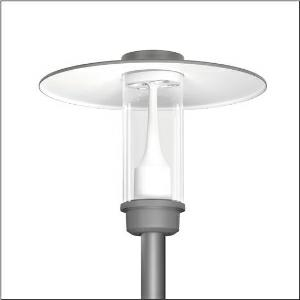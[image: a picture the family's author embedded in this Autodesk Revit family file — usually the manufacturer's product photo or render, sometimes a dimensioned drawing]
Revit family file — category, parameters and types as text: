
# Revit family: litepole_2_iq___st1_2a_5xa5425af14h_a18f
name_source: partatom
category: Lighting Fixtures
units: mm (PartAtom-declared; Revit-internal decimal feet)

## family parameters
Cut with Voids When Loaded = No
Host = Face
Light Source = No
Part Type = Normal
Room Calculation Point = No
Round Connector Dimension = Use Diameter
Shared = No

## types (1)
- --- (1 x LED, 1550 lm, 12.9 W, 2200K)
    Apparent Load = 13 VA
    CIE Flux Codes = 22 60 92 98 100
    Color Rendering = 70
    Color Temperature = 2200K
    Default Elevation = 1800 mm
    Description = Litepole 2 iQ, mast luminaire, Module 540 iQ-SR, primary light control with 3 zone facetted reflector, of plastic, silver coated, highly specular, structured, primary optical cover: cover, of PMMA, transparent, light distribution: ST1.2a, light emission: direct distribution, primary light characteristic: asymmetric, installation type: post-top, LED, High Power LED, rated luminous flux: 1.550lm, luminous efficacy: 120lm/W, light colour: 722, colour temperature: 2200K, control gear: iQ Street-Remote, control: pre-setting: logarithmic dimming characteristic, Street-Remote, Auto-Match, Temp-Guard, Lumen-Switch, Night-Set, Smart-Wire, Light-Fading, Desk-Remote (wireless, voltage-free reading and setting of iQ features in the workshop via application-optimized NFC function/RFID function), optimised constant luminous flux control (CLO 2.0), with terminal, 6-pole, max. 2.5mm², mains connection: 230..240V, AC, 50/60Hz, start of lifetime: 13W, end of service life: 13W, reduction: 6W, luminaire housing, upper part, of aluminium, coated, Siteco® metallic grey (DB 702S), diameter: 750mm, height: 590mm, spigot size: d x l = 76 x 70mm (post-top) | with reducer (optional accessory) 60 x 70mm, mounting height: 3..5m, post-top mast mounting element, of diecast aluminium, coated, Siteco® metallic grey (DB 702S), Module 540 iQ-SR, traffic white (RAL 9016), equipment: standard, protection rating (complete): IP65, insulation class (complete): insulation class II (safety insulation), certification: CE, ENEC, VDE, packaging unit: 1 piece

Light Distribution: ST1.2a
    Height = 590 mm
    Lamp = 1 x LED
    Lamp Light Flux = 1550 lm
    Lamp Power = 12.9 W
    Lamp count = 1
    Length = 750 mm
    Luminous efficacy = 120 lm/W
    Manufacturer = Siteco
    ModVariant = No
    Model = 5XA5425AF14H
    Number of Poles = 1
    OnlyDefault = Yes
    Power Factor = 1
    Product Name = Litepole 2 iQ | ST1.2a
    Product group = mast luminaire | pylon top
    ProductGroupID = 6100
    Protection Class = Protection class II
    Protection Degree = IP 65
    RLX_Detail_Level = 1
    RLX_Emergency_Light_Flux = 0 lm
    RLX_Emergency_Type = 0
    RLX_Emergency_Type_DB = No
    RlxData = <blob elided: 64185 chars, md5=96e908e7>
    Socket = socket
    Standby Power = 0 W
    System Light Flux = 1550 lm
    System Power = 13 W
    Type Comments = factory setting: luminous flux: 100 % | dim-lin: 254 | 516 mA
    Type Image = l_1006518.jpg
    URL = http://relux.com
    VarID = @adj_213975
    Voltage = 0 V
    Weight = 0.00 kg
    Width = 0 mm  [stored 0 ft]

note: [stored X ft] marks values corroborated as IEEE doubles in the binary element streams (Revit-internal decimal feet)

## geometry (parser evidence)
native form markers: Blend x4, Sweep x10
no freeform markers — native parametric forms only
